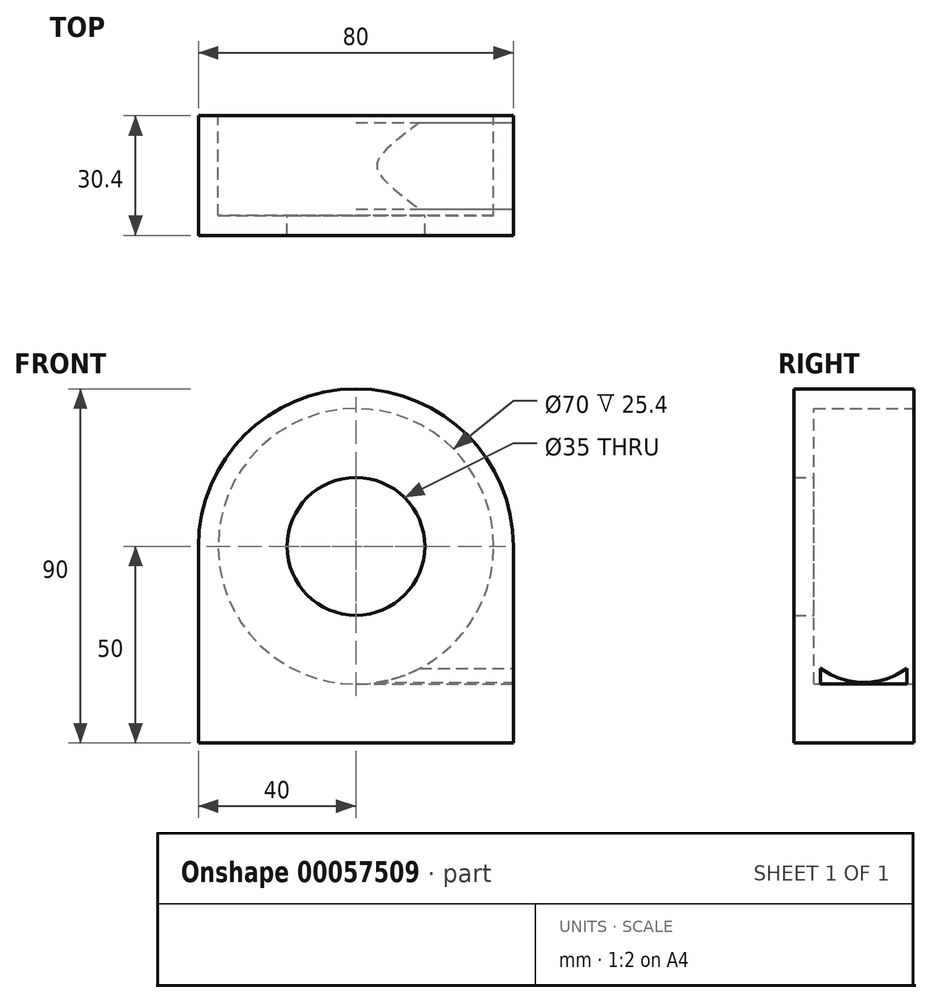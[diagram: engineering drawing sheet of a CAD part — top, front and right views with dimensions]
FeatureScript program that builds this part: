
annotation { "Feature Type Name" : "Feature", "Feature Type Description" : "" }
export const myFeature = defineFeature(function(context is Context, id is Id, definition is map)
    precondition{}
    {
        {
            var Q0;
            Q0=qCreatedBy(makeId("Front.planeOp"),FACE);
            var sketch = newSketch(context, id + "F0", { "sketchPlane" : qUnion([Q0])});
            skArc(sketch, "E0", {"start": v(40, 0) * mm, "mid": v(0, 40) * mm, "end": v(-40, 0) * mm});
            skLineSegment(sketch, "E1", {"start": v(-40, 0) * mm, "end": v(-40, -50) * mm});
            skLineSegment(sketch, "E2.MirrorCS", {"start": v(40, 0) * mm, "end": v(40, -50) * mm});
            skLineSegment(sketch, "E3", {"start": v(-40, -50) * mm, "end": v(40, -50) * mm});
            skCircle(sketch, "E4", {"center": v(0, 0) * mm, "radius": 35 * mm});
            skSolve(sketch);
        }
        {
            var Q0;
            Q0=makeQuery(id+"F0.imprint","IMPRINT",FACE,{"disambiguationData":[TD([[makeQuery(id+"F0.imprint","IMPRINT",EDGE,{"derivedFrom":sQuery(id+"F0.wireOp",EDGE,"E0")}),1.0]])]});
            extrude(context, id + "F1", {"entities" : qUnion([Q0]), "depth" : 25.4 * mm});
        }
        {
            var Q0;
            Q0=makeQuery(id+"F1.opExtrude","CAP_FACE",FACE,{"disambiguationData":[OSD([sQuery(id+"F0.wireOp",EDGE,"E0"),sQuery(id+"F0.wireOp",EDGE,"E1"),sQuery(id+"F0.wireOp",EDGE,"E2.MirrorCS"),sQuery(id+"F0.wireOp",EDGE,"E3"),sQuery(id+"F0.wireOp",EDGE,"E4")])],"isStart":false});
            var sketch = newSketch(context, id + "F2", { "sketchPlane" : qUnion([Q0])});
            skLineSegment(sketch, "E5.bottom", {"start": v(-40, -50) * mm, "end": v(40, -50) * mm});
            skLineSegment(sketch, "E5.top", {"start": v(-40, -25) * mm, "end": v(40, -25) * mm});
            skLineSegment(sketch, "E5.left", {"start": v(-40, -50) * mm, "end": v(-40, -25) * mm});
            skLineSegment(sketch, "E5.right", {"start": v(40, -50) * mm, "end": v(40, -25) * mm});
            skSolve(sketch);
        }
        {
            var Q0;
            Q0=makeQuery(id+"F2.imprint","IMPRINT",FACE,{"disambiguationData":[TD([[makeQuery(id+"F2.imprint","IMPRINT",EDGE,{"derivedFrom":sQuery(id+"F2.wireOp",EDGE,"E5.bottom")}),1.0]])]});
            var Q1;
            {var subQ0=sQuery(id+"F2.wireOp",EDGE,"E5.top");var subQ1=makeQuery(id+"F1.opExtrude","CAP_EDGE",EDGE,{"disambiguationData":[OSD([sQuery(id+"F0.wireOp",EDGE,"E4")])],"isStart":false});var subQ2=makeQuery(id+"F2.imprint","INTERSECT",VERTEX,{"disambiguationData":[OD(0.0)],"derivedFrom":[subQ1,subQ0]});Q1=makeQuery(id+"F2.imprint","IMPRINT",FACE,{"disambiguationData":[TD([[makeQuery(id+"F2.imprint","IMPRINT",EDGE,{"disambiguationData":[TD([[subQ2,-1.0]])],"derivedFrom":subQ0}),-1.0]])]});}
            extrude(context, id + "F3", {"entities" : qUnion([Q0, Q1]), "operationType" : NewBodyOperationType.ADD, "depth" : 25 * mm});
        }
        {
            var Q0;
            Q0=makeQuery(id+"F3.boolean.opBoolean","MERGE",FACE,{"derivedFrom":[makeQuery(id+"F1.opExtrude","SWEPT_FACE",FACE,{"disambiguationData":[OSD([sQuery(id+"F0.wireOp",EDGE,"E2.MirrorCS")])]}),makeQuery(id+"F3.opExtrude","SWEPT_FACE",FACE,{"disambiguationData":[OSD([sQuery(id+"F2.wireOp",EDGE,"E5.right")])]})]});
            var sketch = newSketch(context, id + "F4", { "sketchPlane" : qUnion([Q0])});
            skLineSegment(sketch, "E6", {"start": v(0, -25) * mm, "end": v(-25.4, -25) * mm, "construction": true});
            skLineSegment(sketch, "E7", {"start": v(-25.4, -25) * mm, "end": v(-12.7, -25) * mm, "construction": true});
            skLineSegment(sketch, "E8", {"start": v(-12.7, -25) * mm, "end": v(-12.7, -50) * mm, "construction": true});
            skLineSegment(sketch, "E9.rect.bottom", {"start": v(-1.7, -31) * mm, "end": v(-23.7, -31) * mm, "construction": true});
            skLineSegment(sketch, "E9.rect.top", {"start": v(-1.7, -35) * mm, "end": v(-23.7, -35) * mm});
            skLineSegment(sketch, "E9.rect.left", {"start": v(-1.7, -31) * mm, "end": v(-1.7, -35) * mm});
            skLineSegment(sketch, "E9.rect.right", {"start": v(-23.7, -31) * mm, "end": v(-23.7, -35) * mm});
            skPoint(sketch, "E9.rect.middle", {"position": v(-12.7, -33) * mm});
            skArc(sketch, "E10", {"start": v(-23.7, -31) * mm, "mid": v(-12.7, -34.6) * mm, "end": v(-1.7, -31) * mm});
            skSolve(sketch);
        }
        {
            var Q0;
            Q0 = qSketchRegion(id + "F4", true);
            extrude(context, id + "F5", {"entities" : qUnion([Q0]), "operationType" : NewBodyOperationType.REMOVE, "oppositeDirection" : true, "depth" : 40 * mm});
        }
        {
            var Q0;
            Q0=makeQuery(id+"F1.opExtrude","CAP_FACE",FACE,{"disambiguationData":[OSD([sQuery(id+"F0.wireOp",EDGE,"E0"),sQuery(id+"F0.wireOp",EDGE,"E1"),sQuery(id+"F0.wireOp",EDGE,"E2.MirrorCS"),sQuery(id+"F0.wireOp",EDGE,"E3"),sQuery(id+"F0.wireOp",EDGE,"E4")])],"isStart":false});
            var sketch = newSketch(context, id + "F6", { "sketchPlane" : qUnion([Q0])});
            skCircle(sketch, "E11", {"center": v(0, 0) * mm, "radius": 17.5 * mm});
            skLineSegment(sketch, "E12", {"start": v(-40, -25) * mm, "end": v(40, -25) * mm});
            skLineSegment(sketch, "E13", {"start": v(40, -25) * mm, "end": v(40, 0) * mm});
            skLineSegment(sketch, "E14", {"start": v(-40, -25) * mm, "end": v(-40, 0) * mm});
            skArc(sketch, "E15.trimOffspring", {"start": v(40, 0) * mm, "mid": v(0, 40) * mm, "end": v(-40, 0) * mm});
            skSolve(sketch);
        }
        {
            var Q0;
            Q0 = qSketchRegion(id + "F6", true);
            extrude(context, id + "F7", {"entities" : qUnion([Q0]), "operationType" : NewBodyOperationType.ADD, "depth" : 5 * mm});
        }
        {
            var Q0;
            Q0=makeQuery(id+"F3.opExtrude","CAP_FACE",FACE,{"disambiguationData":[OSD([sQuery(id+"F2.wireOp",EDGE,"E5.bottom"),sQuery(id+"F2.wireOp",EDGE,"E5.top"),sQuery(id+"F2.wireOp",EDGE,"E5.left"),sQuery(id+"F2.wireOp",EDGE,"E5.right")])],"isStart":false});
            extrude(context, id + "F8", {"entities" : qUnion([Q0]), "operationType" : NewBodyOperationType.ADD, "depth" : 5 * mm});
        }
        {
            var Q0;
            {var subQ0=sQuery(id+"F2.wireOp",EDGE,"E5.top");Q0=makeQuery(id+"F8.boolean.opBoolean","MERGE",FACE,{"derivedFrom":[makeQuery(id+"F3.opExtrude","SWEPT_FACE",FACE,{"disambiguationData":[OSD([subQ0])]}),makeQuery(id+"F8.opExtrude","SWEPT_FACE",FACE,{"disambiguationData":[OSD([subQ0])]})]});}
            var sketch = newSketch(context, id + "F9", { "sketchPlane" : qUnion([Q0])});
            skLineSegment(sketch, "E16.bottom", {"start": v(-40, -30.4) * mm, "end": v(40, -30.4) * mm});
            skLineSegment(sketch, "E16.top", {"start": v(-40, -55.4) * mm, "end": v(40, -55.4) * mm});
            skLineSegment(sketch, "E16.left", {"start": v(-40, -30.4) * mm, "end": v(-40, -55.4) * mm});
            skLineSegment(sketch, "E16.right", {"start": v(40, -30.4) * mm, "end": v(40, -55.4) * mm});
            skSolve(sketch);
        }
        {
            var Q0;
            Q0=makeQuery(id+"F9.imprint","IMPRINT",FACE,{"disambiguationData":[TD([[makeQuery(id+"F9.imprint","IMPRINT",EDGE,{"derivedFrom":sQuery(id+"F9.wireOp",EDGE,"E16.bottom")}),-1.0]])]});
            extrude(context, id + "F10", {"entities" : qUnion([Q0]), "operationType" : NewBodyOperationType.REMOVE, "oppositeDirection" : true, "depth" : 25 * mm});
        }
    });
